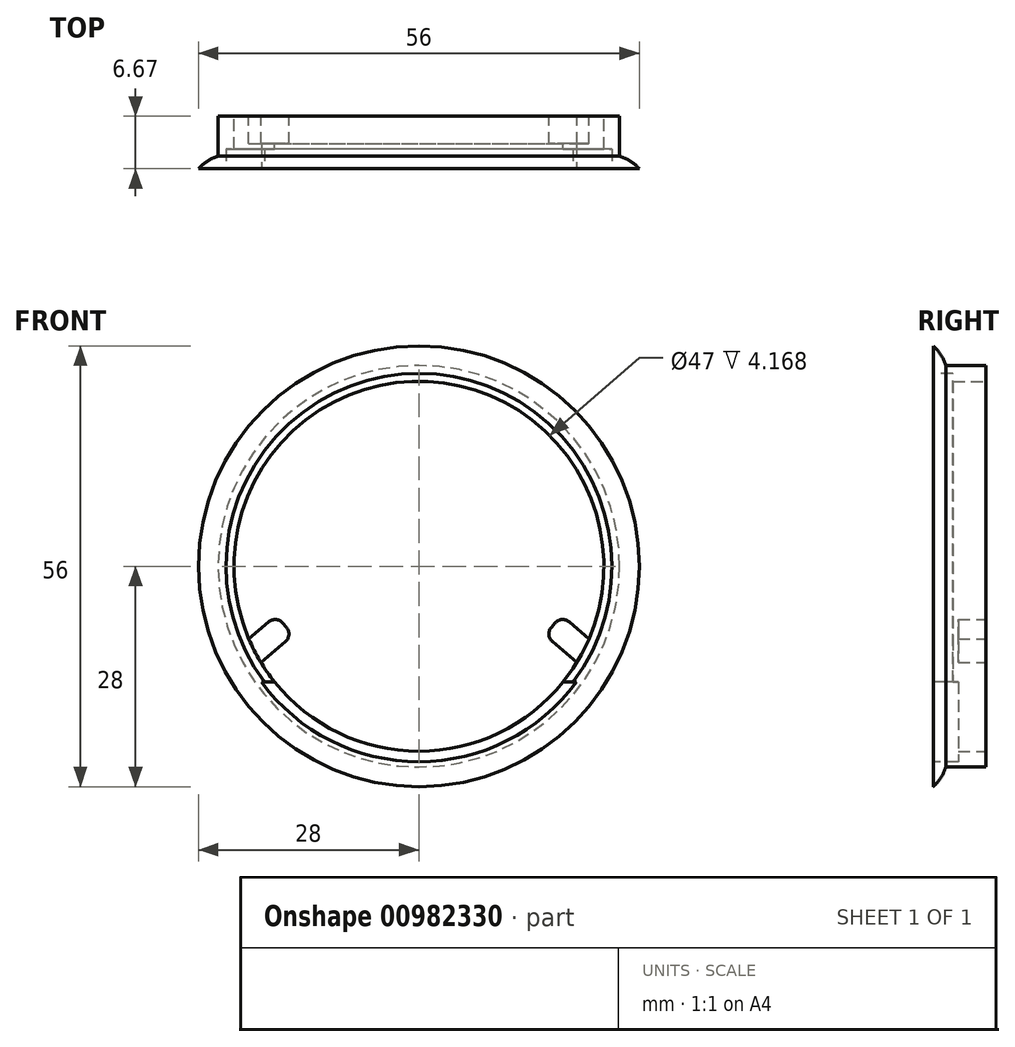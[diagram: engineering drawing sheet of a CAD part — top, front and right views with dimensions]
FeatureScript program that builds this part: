
annotation { "Feature Type Name" : "Feature", "Feature Type Description" : "" }
export const myFeature = defineFeature(function(context is Context, id is Id, definition is map)
    precondition{}
    {
        {
            var Q0;
            Q0=qCreatedBy(makeId("Front.planeOp"),FACE);
            var sketch = newSketch(context, id + "F0", { "sketchPlane" : qUnion([Q0])});
            skCircle(sketch, "E0", {"center": v(0, 0) * mm, "radius": 25.5 * mm});
            skArc(sketch, "E1", {"start": v(-20.06, -12.24) * mm, "mid": v(0, -23.5) * mm, "end": v(20.06, -12.24) * mm});
            skLineSegment(sketch, "E2", {"start": v(-21.61, -9.22) * mm, "end": v(-18.14, -6.24) * mm});
            skLineSegment(sketch, "E3", {"start": v(-18.14, -6.24) * mm, "end": v(-16, -8.75) * mm});
            skLineSegment(sketch, "E4", {"start": v(-16, -8.75) * mm, "end": v(-20.06, -12.24) * mm});
            skLineSegment(sketch, "E5", {"start": v(21.61, -9.22) * mm, "end": v(18.14, -6.24) * mm});
            skLineSegment(sketch, "E6", {"start": v(18.14, -6.24) * mm, "end": v(16, -8.75) * mm});
            skLineSegment(sketch, "E7", {"start": v(16, -8.75) * mm, "end": v(20.06, -12.24) * mm});
            skArc(sketch, "E8.trimOffspring", {"start": v(21.61, -9.22) * mm, "mid": v(0, 23.5) * mm, "end": v(-21.61, -9.22) * mm});
            skSolve(sketch);
        }
        {
            var Q0;
            Q0 = qSketchRegion(id + "F0", true);
            extrude(context, id + "F1", {"entities" : qUnion([Q0]), "depth" : 5.08 * mm, "offsetDistance" : 25.4 * mm});
        }
        {
            var Q0;
            Q0=makeQuery(id+"F1.opExtrude","CAP_FACE",FACE,{"disambiguationData":[OSD([sQuery(id+"F0.wireOp",EDGE,"E0"),sQuery(id+"F0.wireOp",EDGE,"E1"),sQuery(id+"F0.wireOp",EDGE,"E2"),sQuery(id+"F0.wireOp",EDGE,"E3"),sQuery(id+"F0.wireOp",EDGE,"E4"),sQuery(id+"F0.wireOp",EDGE,"E5"),sQuery(id+"F0.wireOp",EDGE,"E6"),sQuery(id+"F0.wireOp",EDGE,"E7"),sQuery(id+"F0.wireOp",EDGE,"E8.trimOffspring")])],"isStart":false});
            var sketch = newSketch(context, id + "F2", { "sketchPlane" : qUnion([Q0])});
            skArc(sketch, "E9", {"start": v(-20, -14.7) * mm, "mid": v(0, -24.83) * mm, "end": v(20, -14.7) * mm});
            skLineSegment(sketch, "E10", {"start": v(20, -14.7) * mm, "end": v(-20, -14.7) * mm});
            skSolve(sketch);
        }
        {
            var Q0;
            Q0=makeQuery(id+"F1.opExtrude","CAP_FACE",FACE,{"disambiguationData":[OSD([sQuery(id+"F0.wireOp",EDGE,"E0"),sQuery(id+"F0.wireOp",EDGE,"E1"),sQuery(id+"F0.wireOp",EDGE,"E2"),sQuery(id+"F0.wireOp",EDGE,"E3"),sQuery(id+"F0.wireOp",EDGE,"E4"),sQuery(id+"F0.wireOp",EDGE,"E5"),sQuery(id+"F0.wireOp",EDGE,"E6"),sQuery(id+"F0.wireOp",EDGE,"E7"),sQuery(id+"F0.wireOp",EDGE,"E8.trimOffspring")])],"isStart":false});
            var sketch = newSketch(context, id + "F3", { "sketchPlane" : qUnion([Q0])});
            skCircle(sketch, "E11", {"center": v(0, 0) * mm, "radius": 23.5 * mm});
            skCircle(sketch, "E12", {"center": v(0, 0) * mm, "radius": 28 * mm});
            skSolve(sketch);
        }
        {
            var Q0;
            Q0 = qSketchRegion(id + "F3", true);
            extrude(context, id + "F4", {"entities" : qUnion([Q0]), "operationType" : NewBodyOperationType.ADD, "depth" : 1.59 * mm, "offsetDistance" : 25.4 * mm});
        }
        {
            var Q0;
            Q0 = qSketchRegion(id + "F2", true);
            extrude(context, id + "F5", {"entities" : qUnion([Q0]), "operationType" : NewBodyOperationType.REMOVE, "oppositeDirection" : true, "depth" : 1.59 * mm, "offsetDistance" : 25.4 * mm, "hasSecondDirection" : true, "secondDirectionOppositeDirection" : false, "secondDirectionDepth" : 3.17 * mm});
        }
        {
            var Q0;
            {var subQ0=sQuery(id+"F0.wireOp",EDGE,"E7");var subQ1=sQuery(id+"F0.wireOp",EDGE,"E5");var subQ2=sQuery(id+"F0.wireOp",EDGE,"E6");var subQ3=sQuery(id+"F0.wireOp",EDGE,"E1");var subQ4=sQuery(id+"F0.wireOp",EDGE,"E8.trimOffspring");Q0=makeQuery(id+"F4.boolean.opBoolean","SPLIT",FACE,{"disambiguationData":[TD([makeQuery(id+"F1.opExtrude","SWEPT_FACE",FACE,{"disambiguationData":[OSD([subQ1])]})])],"derivedFrom":makeQuery(id+"F1.opExtrude","CAP_FACE",FACE,{"disambiguationData":[OSD([sQuery(id+"F0.wireOp",EDGE,"E0"),subQ3,sQuery(id+"F0.wireOp",EDGE,"E2"),sQuery(id+"F0.wireOp",EDGE,"E3"),sQuery(id+"F0.wireOp",EDGE,"E4"),subQ1,subQ2,subQ0,subQ4])],"isStart":false})});}
            var Q1;
            {var subQ0=sQuery(id+"F0.wireOp",EDGE,"E4");var subQ1=sQuery(id+"F0.wireOp",EDGE,"E3");var subQ2=sQuery(id+"F0.wireOp",EDGE,"E2");var subQ3=sQuery(id+"F0.wireOp",EDGE,"E1");var subQ4=sQuery(id+"F0.wireOp",EDGE,"E8.trimOffspring");Q1=makeQuery(id+"F4.boolean.opBoolean","SPLIT",FACE,{"disambiguationData":[TD([makeQuery(id+"F1.opExtrude","SWEPT_FACE",FACE,{"disambiguationData":[OSD([subQ2])]})])],"derivedFrom":makeQuery(id+"F1.opExtrude","CAP_FACE",FACE,{"disambiguationData":[OSD([sQuery(id+"F0.wireOp",EDGE,"E0"),subQ3,subQ2,subQ1,subQ0,sQuery(id+"F0.wireOp",EDGE,"E5"),sQuery(id+"F0.wireOp",EDGE,"E6"),sQuery(id+"F0.wireOp",EDGE,"E7"),subQ4])],"isStart":false})});}
            extrude(context, id + "F6", {"entities" : qUnion([Q0, Q1]), "operationType" : NewBodyOperationType.REMOVE, "oppositeDirection" : true, "depth" : 1.59 * mm, "offsetDistance" : 25.4 * mm});
        }
        {
            var Q0;
            Q0=makeQuery(id+"F4.opExtrude","CAP_EDGE",EDGE,{"disambiguationData":[OSD([sQuery(id+"F3.wireOp",EDGE,"E12")])],"isStart":true});
            chamfer(context, id + "F7", {"entities" : qUnion([Q0]), "width" : 1.59 * mm, "tangentPropagation" : true});
        }
        {
            var Q0;
            {var subQ0=sQuery(id+"F3.wireOp",EDGE,"E12");Q0=makeQuery(id+"F7.opChamfer","BLEND_EDGE",EDGE,{"blendedFrom":[makeQuery(id+"F4.opExtrude","CAP_EDGE",EDGE,{"disambiguationData":[OSD([subQ0])],"isStart":true}),makeQuery(id+"F4.opExtrude","CAP_FACE",FACE,{"disambiguationData":[OSD([sQuery(id+"F3.wireOp",EDGE,"E11"),subQ0])],"isStart":true})],"blendedInto":[makeQuery(id+"F4.opExtrude","CAP_FACE",FACE,{"disambiguationData":[OSD([sQuery(id+"F3.wireOp",EDGE,"E11"),subQ0])],"isStart":true})]});}
            fillet(context, id + "F8", {"entities" : qUnion([Q0]), "radius" : 5.08 * mm, "tangentPropagation" : true, "allowEdgeOverflow" : false});
        }
        {
            var Q0;
            Q0=makeQuery(id+"F4.opExtrude","CAP_FACE",FACE,{"disambiguationData":[OSD([sQuery(id+"F3.wireOp",EDGE,"E11"),sQuery(id+"F3.wireOp",EDGE,"E12")])],"isStart":false});
            var sketch = newSketch(context, id + "F9", { "sketchPlane" : qUnion([Q0])});
            skCircle(sketch, "E13", {"center": v(0, 0) * mm, "radius": 24.5 * mm});
            skSolve(sketch);
        }
        {
            var Q0;
            Q0 = qSketchRegion(id + "F9", true);
            extrude(context, id + "F10", {"entities" : qUnion([Q0]), "operationType" : NewBodyOperationType.REMOVE, "oppositeDirection" : true, "depth" : 2.5 * mm, "offsetDistance" : 25.4 * mm});
        }
        {
            var Q0;
            Q0=makeQuery(id+"F1.opExtrude","SWEPT_EDGE",EDGE,{"disambiguationData":[OSD([sQuery(id+"F0.wireOp",EDGE,"E3"),sQuery(id+"F0.wireOp",EDGE,"E4")])]});
            var Q1;
            Q1=makeQuery(id+"F1.opExtrude","SWEPT_EDGE",EDGE,{"disambiguationData":[OSD([sQuery(id+"F0.wireOp",EDGE,"E2"),sQuery(id+"F0.wireOp",EDGE,"E3")])]});
            var Q2;
            Q2=makeQuery(id+"F1.opExtrude","SWEPT_EDGE",EDGE,{"disambiguationData":[OSD([sQuery(id+"F0.wireOp",EDGE,"E6"),sQuery(id+"F0.wireOp",EDGE,"E7")])]});
            var Q3;
            Q3=makeQuery(id+"F1.opExtrude","SWEPT_EDGE",EDGE,{"disambiguationData":[OSD([sQuery(id+"F0.wireOp",EDGE,"E5"),sQuery(id+"F0.wireOp",EDGE,"E6")])]});
            fillet(context, id + "F11", {"entities" : qUnion([Q0, Q1, Q2, Q3]), "radius" : 1.27 * mm, "tangentPropagation" : true, "allowEdgeOverflow" : false});
        }
    });
